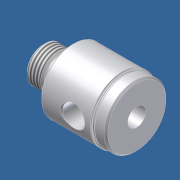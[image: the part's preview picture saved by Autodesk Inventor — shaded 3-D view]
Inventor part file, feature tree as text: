
AUTODESK INVENTOR PART (.ipt)
format: ipt  version: 2012 (Build 160160000, 160)  size: 230,912 bytes
history: native  units: in
note: dims shown in document units (in); Inventor stores cm internally (conversion verified against a paired STEP export)
features: other x106, revolve x5, sketch x5, thread x1
ambient origin geometry x8: Origin, YZ Plane, XZ Plane, XY Plane, X Axis, Y Axis, Z Axis, Center Point
bodies: Solid1 (feature_tree)
feature tree (117):
  other  "09R000_rod_guide"
  revolve  "Revolution1"  [1 undecoded]
  thread  "Thread1"  [1 undecoded]
  revolve  "Revolution2"  Angle=360.0deg
  revolve  "Revolution3"  [1 undecoded]
  revolve  "Revolution4"  [1 undecoded]
  revolve  "Revolution5"  [1 undecoded]
  other  "s1_XY"
  other  "s1_YZ"
  other  "s1_ZX"
  other  "s1_X"
  other  "s1_Y"
  other  "s1_Z"
  other  "s1_Center"
  other  "s2_XY"
  other  "s2_YZ"
  other  "s2_ZX"
  other  "s2_X"
  other  "s2_Y"
  other  "s2_Z"
  other  "s2_Center"
  other  "dp1_XY"
  other  "dp1_YZ"
  other  "dp1_ZX"
  other  "dp1_X"
  other  "dp1_Y"
  other  "dp1_Z"
  other  "dp1_Center"
  other  "dp2_XY"
  other  "dp2_YZ"
  other  "dp2_ZX"
  other  "dp2_X"
  other  "dp2_Y"
  other  "dp2_Z"
  other  "dp2_Center"
  other  "rod_guide_XY"
  other  "rod_guide_YZ"
  other  "rod_guide_ZX"
  other  "rod_guide_X"
  other  "rod_guide_Y"
  other  "rod_guide_Z"
  other  "rod_guide_Center"
  other  "to_tube_XY"
  other  "to_tube_YZ"
  other  "to_tube_ZX"
  other  "to_tube_X"
  other  "to_tube_Y"
  other  "to_tube_Z"
  other  "to_tube_Center"
  other  "to_foot_bracket_XY"
  other  "to_foot_bracket_YZ"
  other  "to_foot_bracket_ZX"
  other  "to_foot_bracket_X"
  other  "to_foot_bracket_Y"
  other  "to_foot_bracket_Z"
  other  "to_foot_bracket_Center"
  other  "to_nut_XY"
  other  "to_nut_YZ"
  other  "to_nut_ZX"
  other  "to_nut_X"
  other  "to_nut_Y"
  other  "to_nut_Z"
  other  "to_nut_Center"
  other  "to_trunnion_brackets_XY"
  other  "to_trunnion_brackets_YZ"
  other  "to_trunnion_brackets_ZX"
  other  "to_trunnion_brackets_X"
  other  "to_trunnion_brackets_Y"
  other  "to_trunnion_brackets_Z"
  other  "to_trunnion_brackets_Center"
  other  "to_trunnion_brackets1_XY"
  other  "to_trunnion_brackets1_YZ"
  other  "to_trunnion_brackets1_ZX"
  other  "to_trunnion_brackets1_X"
  other  "to_trunnion_brackets1_Y"
  other  "to_trunnion_brackets1_Z"
  other  "to_trunnion_brackets1_Center"
  other  "to_trunnion_brackets2_XY"
  other  "to_trunnion_brackets2_YZ"
  other  "to_trunnion_brackets2_ZX"
  other  "to_trunnion_brackets2_X"
  other  "to_trunnion_brackets2_Y"
  other  "to_trunnion_brackets2_Z"
  other  "to_trunnion_brackets2_Center"
  other  "t111_XY"
  other  "t111_YZ"
  other  "t111_ZX"
  other  "t111_X"
  other  "t111_Y"
  other  "t111_Z"
  other  "t111_Center"
  other  "t1_XY"
  other  "t1_YZ"
  other  "t1_ZX"
  other  "t1_X"
  other  "t1_Y"
  other  "t1_Z"
  other  "t1_Center"
  other  "port_XY"
  other  "port_YZ"
  other  "port_ZX"
  other  "port_X"
  other  "port_Y"
  other  "port_Z"
  other  "port_Center"
  other  "to_screw_XY"
  other  "to_screw_YZ"
  other  "to_screw_ZX"
  other  "to_screw_X"
  other  "to_screw_Y"
  other  "to_screw_Z"
  other  "to_screw_Center"
  sketch  "Sketch_2"  dims[d0=360.0deg d1=0.2958in d2=0.0in d3=360.0deg]
  sketch  "Sketch_3"  dims[d4=360.0deg d5=360.0deg]
  sketch  "Sketch_5"  dims[d6=360.0deg]
  sketch  "Sketch_40"
  sketch  "Sketch_47"
note: 5 required parameter values undecoded (feature->parameter linkage not recoverable at this tier; creation-order binding heuristic only, values carry confidence <= 0.55)